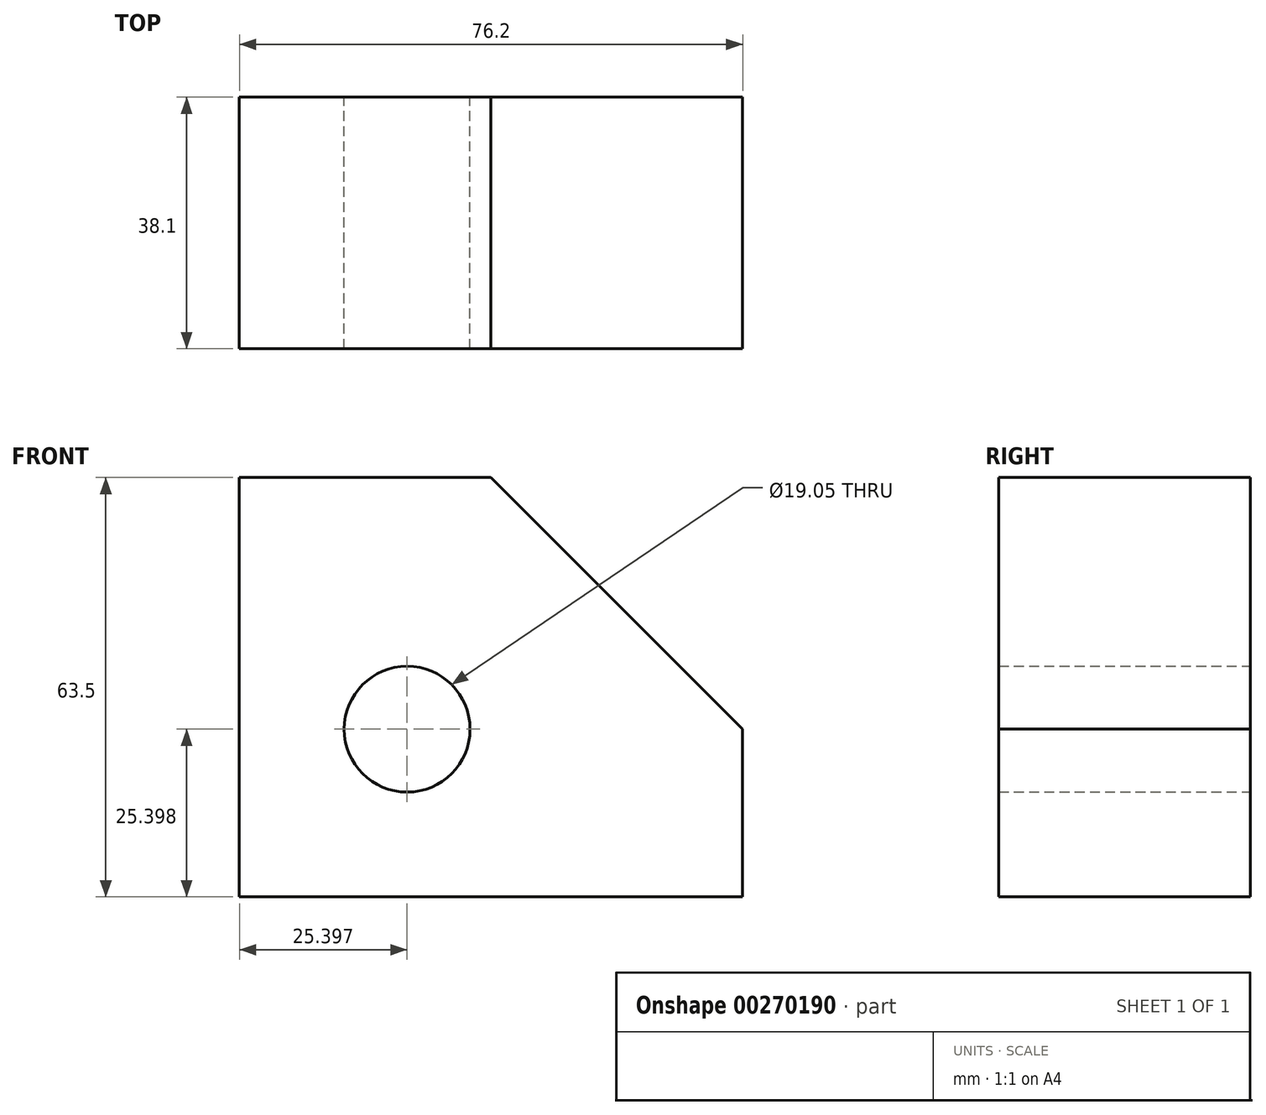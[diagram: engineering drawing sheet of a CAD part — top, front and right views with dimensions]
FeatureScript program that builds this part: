
annotation { "Feature Type Name" : "Feature", "Feature Type Description" : "" }
export const myFeature = defineFeature(function(context is Context, id is Id, definition is map)
    precondition{}
    {
        {
            var Q0;
            Q0=qCreatedBy(makeId("Front.planeOp"),FACE);
            var sketch = newSketch(context, id + "F0", { "sketchPlane" : qUnion([Q0])});
            skLineSegment(sketch, "E0", {"start": v(-48.62, 28.79) * mm, "end": v(-48.62, -34.71) * mm});
            skLineSegment(sketch, "E1", {"start": v(-48.62, -34.71) * mm, "end": v(27.58, -34.71) * mm});
            skLineSegment(sketch, "E2", {"start": v(27.58, -34.71) * mm, "end": v(27.58, -9.31) * mm});
            skLineSegment(sketch, "E3", {"start": v(27.58, -9.31) * mm, "end": v(-10.52, 28.79) * mm});
            skLineSegment(sketch, "E4", {"start": v(-10.52, 28.79) * mm, "end": v(-48.62, 28.79) * mm});
            skCircle(sketch, "E5", {"center": v(-23.22, -9.31) * mm, "radius": 9.53 * mm});
            skSolve(sketch);
        }
        {
            var Q0;
            Q0=qSketchRegion(id+"F0",true);
            extrude(context, id + "F1", {"entities" : qUnion([Q0]), "depth" : 38.1 * mm, "symmetric" : true});
        }
    });
